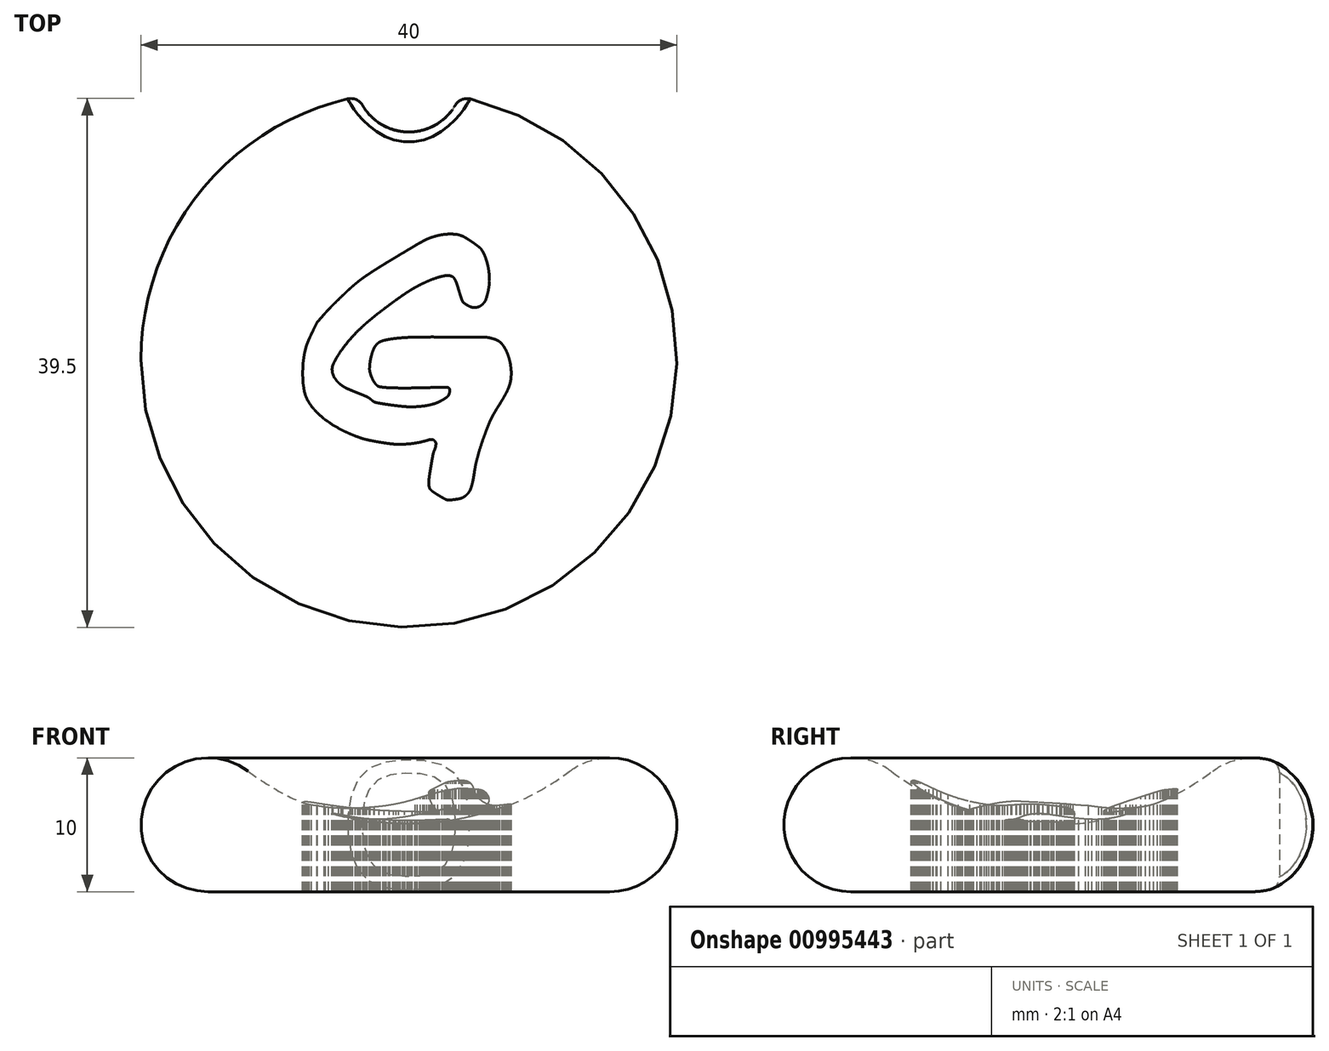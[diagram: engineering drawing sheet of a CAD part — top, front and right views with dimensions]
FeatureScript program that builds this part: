
annotation { "Feature Type Name" : "Feature", "Feature Type Description" : "" }
export const myFeature = defineFeature(function(context is Context, id is Id, definition is map)
    precondition{}
    {
        {
            var Q0;
            Q0=qCreatedBy(makeId("Front.planeOp"),FACE);
            var sketch = newSketch(context, id + "F0", { "sketchPlane" : qUnion([Q0])});
            skArc(sketch, "E0", {"start": v(-12, 9) * mm, "mid": v(-19.74, 6.58) * mm, "end": v(-15, 0) * mm});
            skArc(sketch, "E1", {"start": v(-12, 9) * mm, "mid": v(-6.32, 6.03) * mm, "end": v(0, 5) * mm});
            skLineSegment(sketch, "E2", {"start": v(-15, 0) * mm, "end": v(0, 0) * mm});
            skLineSegment(sketch, "E3", {"start": v(0, 0) * mm, "end": v(0, 5) * mm});
            skSolve(sketch);
        }
        {
            var Q0;
            Q0=makeQuery(id+"F0.imprint","IMPRINT",FACE,{"disambiguationData":[TD([[makeQuery(id+"F0.imprint","IMPRINT",EDGE,{"derivedFrom":sQuery(id+"F0.wireOp",EDGE,"E0")}),1.0]])]});
            var Q1;
            Q1=sQuery(id+"F0.wireOp",EDGE,"E3");
            revolve(context, id + "F1", {"surfaceOperationType" : NewSurfaceOperationType.NEW, "entities" : qUnion([Q0]), "axis" : qUnion([Q1]), "revolveType" : RevolveType.FULL});
        }
        {
            var Q0;
            Q0=qCreatedBy(makeId("Top.planeOp"),FACE);
            cPlane(context, id + "F2", {"entities" : qUnion([Q0]), "cplaneType" : CPlaneType.OFFSET, "offset" : 10 * mm, "width" : 150 * mm, "height" : 150 * mm});
        }
        {
            var Q0;
            Q0=qCreatedBy(id+"F2.planeOp",FACE);
            var sketch = newSketch(context, id + "F3", { "sketchPlane" : qUnion([Q0])});
            skLineSegment(sketch, "E4", {"start": v(-4381.95, 0) * mm, "end": v(-4381.95, -4381.95) * mm});
            skLineSegment(sketch, "E5", {"start": v(-4381.95, -4381.95) * mm, "end": v(0, -4381.95) * mm});
            skLineSegment(sketch, "E6", {"start": v(0, -4381.95) * mm, "end": v(4381.95, -4381.95) * mm});
            skLineSegment(sketch, "E7", {"start": v(4381.95, -4381.95) * mm, "end": v(4381.95, 0) * mm});
            skLineSegment(sketch, "E8", {"start": v(4381.95, 0) * mm, "end": v(4381.95, 4381.95) * mm});
            skLineSegment(sketch, "E9", {"start": v(4381.95, 4381.95) * mm, "end": v(0, 4381.95) * mm});
            skLineSegment(sketch, "E10", {"start": v(0, 4381.95) * mm, "end": v(-4381.95, 4381.95) * mm});
            skLineSegment(sketch, "E11", {"start": v(-4381.95, 4381.95) * mm, "end": v(-4381.95, 0) * mm});
            skLineSegment(sketch, "E12", {"start": v(3.49, 9.37) * mm, "end": v(3.47, 9.37) * mm});
            skLineSegment(sketch, "E13", {"start": v(3.47, 9.37) * mm, "end": v(3.43, 9.37) * mm});
            skLineSegment(sketch, "E14", {"start": v(3.43, 9.37) * mm, "end": v(3.34, 9.37) * mm});
            skLineSegment(sketch, "E15", {"start": v(3.34, 9.37) * mm, "end": v(3.23, 9.37) * mm});
            skLineSegment(sketch, "E16", {"start": v(3.23, 9.37) * mm, "end": v(3.14, 9.37) * mm});
            skLineSegment(sketch, "E17", {"start": v(3.14, 9.37) * mm, "end": v(3.12, 9.38) * mm});
            skLineSegment(sketch, "E18", {"start": v(3.12, 9.38) * mm, "end": v(3, 9.38) * mm});
            skLineSegment(sketch, "E19", {"start": v(3, 9.38) * mm, "end": v(2.65, 9.36) * mm});
            skLineSegment(sketch, "E20", {"start": v(2.65, 9.36) * mm, "end": v(2.17, 9.27) * mm});
            skLineSegment(sketch, "E21", {"start": v(2.17, 9.27) * mm, "end": v(1.68, 9.13) * mm});
            skLineSegment(sketch, "E22", {"start": v(1.68, 9.13) * mm, "end": v(1.33, 8.99) * mm});
            skLineSegment(sketch, "E23", {"start": v(1.33, 8.99) * mm, "end": v(1.22, 8.93) * mm});
            skLineSegment(sketch, "E24", {"start": v(1.22, 8.93) * mm, "end": v(1.18, 8.91) * mm});
            skLineSegment(sketch, "E25", {"start": v(1.18, 8.91) * mm, "end": v(1.06, 8.85) * mm});
            skLineSegment(sketch, "E26", {"start": v(1.06, 8.85) * mm, "end": v(0.85, 8.74) * mm});
            skLineSegment(sketch, "E27", {"start": v(0.85, 8.74) * mm, "end": v(0.63, 8.6) * mm});
            skLineSegment(sketch, "E28", {"start": v(0.63, 8.6) * mm, "end": v(0.46, 8.51) * mm});
            skLineSegment(sketch, "E29", {"start": v(0.46, 8.51) * mm, "end": v(0.41, 8.48) * mm});
            skLineSegment(sketch, "E30", {"start": v(0.41, 8.48) * mm, "end": v(0.24, 8.38) * mm});
            skLineSegment(sketch, "E31", {"start": v(0.24, 8.38) * mm, "end": v(-0.26, 8.08) * mm});
            skLineSegment(sketch, "E32", {"start": v(-0.26, 8.08) * mm, "end": v(-0.85, 7.73) * mm});
            skLineSegment(sketch, "E33", {"start": v(-0.85, 7.73) * mm, "end": v(-1.37, 7.41) * mm});
            skLineSegment(sketch, "E34", {"start": v(-1.37, 7.41) * mm, "end": v(-1.83, 7.13) * mm});
            skLineSegment(sketch, "E35", {"start": v(-1.83, 7.13) * mm, "end": v(-2.23, 6.89) * mm});
            skLineSegment(sketch, "E36", {"start": v(-2.23, 6.89) * mm, "end": v(-2.57, 6.67) * mm});
            skLineSegment(sketch, "E37", {"start": v(-2.57, 6.67) * mm, "end": v(-2.88, 6.47) * mm});
            skLineSegment(sketch, "E38", {"start": v(-2.88, 6.47) * mm, "end": v(-3.15, 6.3) * mm});
            skLineSegment(sketch, "E39", {"start": v(-3.15, 6.3) * mm, "end": v(-3.4, 6.12) * mm});
            skLineSegment(sketch, "E40", {"start": v(-3.4, 6.12) * mm, "end": v(-3.6, 5.96) * mm});
            skLineSegment(sketch, "E41", {"start": v(-3.6, 5.96) * mm, "end": v(-3.8, 5.8) * mm});
            skLineSegment(sketch, "E42", {"start": v(-3.8, 5.8) * mm, "end": v(-4, 5.65) * mm});
            skLineSegment(sketch, "E43", {"start": v(-4, 5.65) * mm, "end": v(-4.19, 5.49) * mm});
            skLineSegment(sketch, "E44", {"start": v(-4.19, 5.49) * mm, "end": v(-4.38, 5.32) * mm});
            skLineSegment(sketch, "E45", {"start": v(-4.38, 5.32) * mm, "end": v(-4.59, 5.13) * mm});
            skLineSegment(sketch, "E46", {"start": v(-4.59, 5.13) * mm, "end": v(-4.75, 4.97) * mm});
            skLineSegment(sketch, "E47", {"start": v(-4.75, 4.97) * mm, "end": v(-4.8, 4.92) * mm});
            skLineSegment(sketch, "E48", {"start": v(-4.8, 4.92) * mm, "end": v(-4.92, 4.82) * mm});
            skLineSegment(sketch, "E49", {"start": v(-4.92, 4.82) * mm, "end": v(-5.25, 4.5) * mm});
            skLineSegment(sketch, "E50", {"start": v(-5.25, 4.5) * mm, "end": v(-5.65, 4.1) * mm});
            skLineSegment(sketch, "E51", {"start": v(-5.65, 4.1) * mm, "end": v(-6, 3.73) * mm});
            skLineSegment(sketch, "E52", {"start": v(-6, 3.73) * mm, "end": v(-6.23, 3.48) * mm});
            skLineSegment(sketch, "E53", {"start": v(-6.23, 3.48) * mm, "end": v(-6.3, 3.4) * mm});
            skLineSegment(sketch, "E54", {"start": v(-6.3, 3.4) * mm, "end": v(-6.87, 2.75) * mm});
            skLineSegment(sketch, "E55", {"start": v(-6.87, 2.75) * mm, "end": v(-7.17, 2.13) * mm});
            skLineSegment(sketch, "E56", {"start": v(-7.17, 2.13) * mm, "end": v(-7.2, 2.06) * mm});
            skLineSegment(sketch, "E57", {"start": v(-7.2, 2.06) * mm, "end": v(-7.3, 1.84) * mm});
            skLineSegment(sketch, "E58", {"start": v(-7.3, 1.84) * mm, "end": v(-7.42, 1.6) * mm});
            skLineSegment(sketch, "E59", {"start": v(-7.42, 1.6) * mm, "end": v(-7.5, 1.4) * mm});
            skLineSegment(sketch, "E60", {"start": v(-7.5, 1.4) * mm, "end": v(-7.57, 1.23) * mm});
            skLineSegment(sketch, "E61", {"start": v(-7.57, 1.23) * mm, "end": v(-7.63, 1.07) * mm});
            skLineSegment(sketch, "E62", {"start": v(-7.63, 1.07) * mm, "end": v(-7.68, 0.92) * mm});
            skLineSegment(sketch, "E63", {"start": v(-7.68, 0.92) * mm, "end": v(-7.72, 0.75) * mm});
            skLineSegment(sketch, "E64", {"start": v(-7.72, 0.75) * mm, "end": v(-7.76, 0.6) * mm});
            skLineSegment(sketch, "E65", {"start": v(-7.76, 0.6) * mm, "end": v(-7.77, 0.56) * mm});
            skLineSegment(sketch, "E66", {"start": v(-7.77, 0.56) * mm, "end": v(-7.81, 0.37) * mm});
            skLineSegment(sketch, "E67", {"start": v(-7.81, 0.37) * mm, "end": v(-7.9, -0.22) * mm});
            skLineSegment(sketch, "E68", {"start": v(-7.9, -0.22) * mm, "end": v(-7.93, -1.05) * mm});
            skLineSegment(sketch, "E69", {"start": v(-7.93, -1.05) * mm, "end": v(-7.89, -1.84) * mm});
            skLineSegment(sketch, "E70", {"start": v(-7.89, -1.84) * mm, "end": v(-7.8, -2.37) * mm});
            skLineSegment(sketch, "E71", {"start": v(-7.8, -2.37) * mm, "end": v(-7.76, -2.54) * mm});
            skLineSegment(sketch, "E72", {"start": v(-7.76, -2.54) * mm, "end": v(-7.72, -2.67) * mm});
            skLineSegment(sketch, "E73", {"start": v(-7.72, -2.67) * mm, "end": v(-7.57, -3.03) * mm});
            skLineSegment(sketch, "E74", {"start": v(-7.57, -3.03) * mm, "end": v(-7.26, -3.51) * mm});
            skLineSegment(sketch, "E75", {"start": v(-7.26, -3.51) * mm, "end": v(-6.84, -3.98) * mm});
            skLineSegment(sketch, "E76", {"start": v(-6.84, -3.98) * mm, "end": v(-6.33, -4.43) * mm});
            skLineSegment(sketch, "E77", {"start": v(-6.33, -4.43) * mm, "end": v(-5.73, -4.85) * mm});
            skLineSegment(sketch, "E78", {"start": v(-5.73, -4.85) * mm, "end": v(-5.05, -5.24) * mm});
            skLineSegment(sketch, "E79", {"start": v(-5.05, -5.24) * mm, "end": v(-4.3, -5.6) * mm});
            skLineSegment(sketch, "E80", {"start": v(-4.3, -5.6) * mm, "end": v(-3.7, -5.82) * mm});
            skLineSegment(sketch, "E81", {"start": v(-3.7, -5.82) * mm, "end": v(-3.49, -5.9) * mm});
            skLineSegment(sketch, "E82", {"start": v(-3.49, -5.9) * mm, "end": v(-3.43, -5.91) * mm});
            skLineSegment(sketch, "E83", {"start": v(-3.43, -5.91) * mm, "end": v(-3.26, -5.96) * mm});
            skLineSegment(sketch, "E84", {"start": v(-3.26, -5.96) * mm, "end": v(-2.95, -6.03) * mm});
            skLineSegment(sketch, "E85", {"start": v(-2.95, -6.03) * mm, "end": v(-2.6, -6.1) * mm});
            skLineSegment(sketch, "E86", {"start": v(-2.6, -6.1) * mm, "end": v(-2.22, -6.16) * mm});
            skLineSegment(sketch, "E87", {"start": v(-2.22, -6.16) * mm, "end": v(-1.83, -6.23) * mm});
            skLineSegment(sketch, "E88", {"start": v(-1.83, -6.23) * mm, "end": v(-1.47, -6.28) * mm});
            skLineSegment(sketch, "E89", {"start": v(-1.47, -6.28) * mm, "end": v(-1.15, -6.31) * mm});
            skLineSegment(sketch, "E90", {"start": v(-1.15, -6.31) * mm, "end": v(-0.97, -6.33) * mm});
            skLineSegment(sketch, "E91", {"start": v(-0.97, -6.33) * mm, "end": v(-0.9, -6.33) * mm});
            skLineSegment(sketch, "E92", {"start": v(-0.9, -6.33) * mm, "end": v(-0.76, -6.33) * mm});
            skLineSegment(sketch, "E93", {"start": v(-0.76, -6.33) * mm, "end": v(-0.31, -6.32) * mm});
            skLineSegment(sketch, "E94", {"start": v(-0.31, -6.32) * mm, "end": v(0.25, -6.28) * mm});
            skLineSegment(sketch, "E95", {"start": v(0.25, -6.28) * mm, "end": v(0.78, -6.19) * mm});
            skLineSegment(sketch, "E96", {"start": v(0.78, -6.19) * mm, "end": v(1.19, -6.09) * mm});
            skLineSegment(sketch, "E97", {"start": v(1.19, -6.09) * mm, "end": v(1.32, -6.05) * mm});
            skLineSegment(sketch, "E98", {"start": v(1.32, -6.05) * mm, "end": v(1.37, -6.04) * mm});
            skLineSegment(sketch, "E99", {"start": v(1.37, -6.04) * mm, "end": v(1.5, -6) * mm});
            skLineSegment(sketch, "E100", {"start": v(1.5, -6) * mm, "end": v(1.63, -5.97) * mm});
            skLineSegment(sketch, "E101", {"start": v(1.63, -5.97) * mm, "end": v(1.73, -5.97) * mm});
            skLineSegment(sketch, "E102", {"start": v(1.73, -5.97) * mm, "end": v(1.78, -5.98) * mm});
            skLineSegment(sketch, "E103", {"start": v(1.78, -5.98) * mm, "end": v(1.8, -5.99) * mm});
            skLineSegment(sketch, "E104", {"start": v(1.8, -5.99) * mm, "end": v(1.84, -6) * mm});
            skLineSegment(sketch, "E105", {"start": v(1.84, -6) * mm, "end": v(1.95, -6.09) * mm});
            skLineSegment(sketch, "E106", {"start": v(1.95, -6.09) * mm, "end": v(2.02, -6.25) * mm});
            skLineSegment(sketch, "E107", {"start": v(2.02, -6.25) * mm, "end": v(2.01, -6.47) * mm});
            skLineSegment(sketch, "E108", {"start": v(2.01, -6.47) * mm, "end": v(1.95, -6.66) * mm});
            skLineSegment(sketch, "E109", {"start": v(1.95, -6.66) * mm, "end": v(1.92, -6.72) * mm});
            skLineSegment(sketch, "E110", {"start": v(1.92, -6.72) * mm, "end": v(1.92, -6.74) * mm});
            skLineSegment(sketch, "E111", {"start": v(1.92, -6.74) * mm, "end": v(1.9, -6.8) * mm});
            skLineSegment(sketch, "E112", {"start": v(1.9, -6.8) * mm, "end": v(1.86, -6.87) * mm});
            skLineSegment(sketch, "E113", {"start": v(1.86, -6.87) * mm, "end": v(1.83, -6.97) * mm});
            skLineSegment(sketch, "E114", {"start": v(1.83, -6.97) * mm, "end": v(1.8, -7.09) * mm});
            skLineSegment(sketch, "E115", {"start": v(1.8, -7.09) * mm, "end": v(1.78, -7.24) * mm});
            skLineSegment(sketch, "E116", {"start": v(1.78, -7.24) * mm, "end": v(1.74, -7.43) * mm});
            skLineSegment(sketch, "E117", {"start": v(1.74, -7.43) * mm, "end": v(1.7, -7.67) * mm});
            skLineSegment(sketch, "E118", {"start": v(1.7, -7.67) * mm, "end": v(1.66, -7.9) * mm});
            skLineSegment(sketch, "E119", {"start": v(1.66, -7.9) * mm, "end": v(1.65, -7.98) * mm});
            skLineSegment(sketch, "E120", {"start": v(1.65, -7.98) * mm, "end": v(1.63, -8.07) * mm});
            skLineSegment(sketch, "E121", {"start": v(1.63, -8.07) * mm, "end": v(1.59, -8.34) * mm});
            skLineSegment(sketch, "E122", {"start": v(1.59, -8.34) * mm, "end": v(1.54, -8.64) * mm});
            skLineSegment(sketch, "E123", {"start": v(1.54, -8.64) * mm, "end": v(1.5, -8.88) * mm});
            skLineSegment(sketch, "E124", {"start": v(1.5, -8.88) * mm, "end": v(1.5, -9.06) * mm});
            skLineSegment(sketch, "E125", {"start": v(1.5, -9.06) * mm, "end": v(1.48, -9.21) * mm});
            skLineSegment(sketch, "E126", {"start": v(1.48, -9.21) * mm, "end": v(1.49, -9.34) * mm});
            skLineSegment(sketch, "E127", {"start": v(1.49, -9.34) * mm, "end": v(1.5, -9.44) * mm});
            skLineSegment(sketch, "E128", {"start": v(1.5, -9.44) * mm, "end": v(1.52, -9.52) * mm});
            skLineSegment(sketch, "E129", {"start": v(1.52, -9.52) * mm, "end": v(1.53, -9.55) * mm});
            skLineSegment(sketch, "E130", {"start": v(1.53, -9.55) * mm, "end": v(1.54, -9.57) * mm});
            skLineSegment(sketch, "E131", {"start": v(1.54, -9.57) * mm, "end": v(1.56, -9.64) * mm});
            skLineSegment(sketch, "E132", {"start": v(1.56, -9.64) * mm, "end": v(1.61, -9.72) * mm});
            skLineSegment(sketch, "E133", {"start": v(1.61, -9.72) * mm, "end": v(1.7, -9.8) * mm});
            skLineSegment(sketch, "E134", {"start": v(1.7, -9.8) * mm, "end": v(1.8, -9.88) * mm});
            skLineSegment(sketch, "E135", {"start": v(1.8, -9.88) * mm, "end": v(1.85, -9.9) * mm});
            skLineSegment(sketch, "E136", {"start": v(1.85, -9.9) * mm, "end": v(1.92, -9.96) * mm});
            skLineSegment(sketch, "E137", {"start": v(1.92, -9.96) * mm, "end": v(2.16, -10.11) * mm});
            skLineSegment(sketch, "E138", {"start": v(2.16, -10.11) * mm, "end": v(2.47, -10.3) * mm});
            skLineSegment(sketch, "E139", {"start": v(2.47, -10.3) * mm, "end": v(2.72, -10.43) * mm});
            skLineSegment(sketch, "E140", {"start": v(2.72, -10.43) * mm, "end": v(2.84, -10.49) * mm});
            skLineSegment(sketch, "E141", {"start": v(2.84, -10.49) * mm, "end": v(2.88, -10.5) * mm});
            skLineSegment(sketch, "E142", {"start": v(2.88, -10.5) * mm, "end": v(2.9, -10.5) * mm});
            skLineSegment(sketch, "E143", {"start": v(2.9, -10.5) * mm, "end": v(2.97, -10.5) * mm});
            skLineSegment(sketch, "E144", {"start": v(2.97, -10.5) * mm, "end": v(3.1, -10.49) * mm});
            skLineSegment(sketch, "E145", {"start": v(3.1, -10.49) * mm, "end": v(3.28, -10.47) * mm});
            skLineSegment(sketch, "E146", {"start": v(3.28, -10.47) * mm, "end": v(3.43, -10.45) * mm});
            skLineSegment(sketch, "E147", {"start": v(3.43, -10.45) * mm, "end": v(3.47, -10.45) * mm});
            skLineSegment(sketch, "E148", {"start": v(3.47, -10.45) * mm, "end": v(3.54, -10.44) * mm});
            skLineSegment(sketch, "E149", {"start": v(3.54, -10.44) * mm, "end": v(3.74, -10.4) * mm});
            skLineSegment(sketch, "E150", {"start": v(3.74, -10.4) * mm, "end": v(3.9, -10.36) * mm});
            skLineSegment(sketch, "E151", {"start": v(3.9, -10.36) * mm, "end": v(4.03, -10.3) * mm});
            skLineSegment(sketch, "E152", {"start": v(4.03, -10.3) * mm, "end": v(4.13, -10.24) * mm});
            skLineSegment(sketch, "E153", {"start": v(4.13, -10.24) * mm, "end": v(4.17, -10.22) * mm});
            skLineSegment(sketch, "E154", {"start": v(4.17, -10.22) * mm, "end": v(4.2, -10.2) * mm});
            skLineSegment(sketch, "E155", {"start": v(4.2, -10.2) * mm, "end": v(4.3, -10.11) * mm});
            skLineSegment(sketch, "E156", {"start": v(4.3, -10.11) * mm, "end": v(4.43, -9.99) * mm});
            skLineSegment(sketch, "E157", {"start": v(4.43, -9.99) * mm, "end": v(4.53, -9.84) * mm});
            skLineSegment(sketch, "E158", {"start": v(4.53, -9.84) * mm, "end": v(4.62, -9.66) * mm});
            skLineSegment(sketch, "E159", {"start": v(4.62, -9.66) * mm, "end": v(4.7, -9.43) * mm});
            skLineSegment(sketch, "E160", {"start": v(4.7, -9.43) * mm, "end": v(4.76, -9.16) * mm});
            skLineSegment(sketch, "E161", {"start": v(4.76, -9.16) * mm, "end": v(4.82, -8.84) * mm});
            skLineSegment(sketch, "E162", {"start": v(4.82, -8.84) * mm, "end": v(4.87, -8.55) * mm});
            skLineSegment(sketch, "E163", {"start": v(4.87, -8.55) * mm, "end": v(4.88, -8.46) * mm});
            skLineSegment(sketch, "E164", {"start": v(4.88, -8.46) * mm, "end": v(4.9, -8.28) * mm});
            skLineSegment(sketch, "E165", {"start": v(4.9, -8.28) * mm, "end": v(5, -7.74) * mm});
            skLineSegment(sketch, "E166", {"start": v(5, -7.74) * mm, "end": v(5.2, -6.98) * mm});
            skLineSegment(sketch, "E167", {"start": v(5.2, -6.98) * mm, "end": v(5.48, -6.12) * mm});
            skLineSegment(sketch, "E168", {"start": v(5.48, -6.12) * mm, "end": v(5.75, -5.36) * mm});
            skLineSegment(sketch, "E169", {"start": v(5.75, -5.36) * mm, "end": v(5.85, -5.1) * mm});
            skLineSegment(sketch, "E170", {"start": v(5.85, -5.1) * mm, "end": v(5.87, -5.05) * mm});
            skLineSegment(sketch, "E171", {"start": v(5.87, -5.05) * mm, "end": v(5.94, -4.88) * mm});
            skLineSegment(sketch, "E172", {"start": v(5.94, -4.88) * mm, "end": v(6.02, -4.68) * mm});
            skLineSegment(sketch, "E173", {"start": v(6.02, -4.68) * mm, "end": v(6.1, -4.5) * mm});
            skLineSegment(sketch, "E174", {"start": v(6.1, -4.5) * mm, "end": v(6.2, -4.3) * mm});
            skLineSegment(sketch, "E175", {"start": v(6.2, -4.3) * mm, "end": v(6.3, -4.12) * mm});
            skLineSegment(sketch, "E176", {"start": v(6.3, -4.12) * mm, "end": v(6.42, -3.9) * mm});
            skLineSegment(sketch, "E177", {"start": v(6.42, -3.9) * mm, "end": v(6.57, -3.67) * mm});
            skLineSegment(sketch, "E178", {"start": v(6.57, -3.67) * mm, "end": v(6.7, -3.46) * mm});
            skLineSegment(sketch, "E179", {"start": v(6.7, -3.46) * mm, "end": v(6.74, -3.39) * mm});
            skLineSegment(sketch, "E180", {"start": v(6.74, -3.39) * mm, "end": v(6.8, -3.29) * mm});
            skLineSegment(sketch, "E181", {"start": v(6.8, -3.29) * mm, "end": v(7, -2.98) * mm});
            skLineSegment(sketch, "E182", {"start": v(7, -2.98) * mm, "end": v(7.2, -2.63) * mm});
            skLineSegment(sketch, "E183", {"start": v(7.2, -2.63) * mm, "end": v(7.35, -2.32) * mm});
            skLineSegment(sketch, "E184", {"start": v(7.35, -2.32) * mm, "end": v(7.47, -2.05) * mm});
            skLineSegment(sketch, "E185", {"start": v(7.47, -2.05) * mm, "end": v(7.55, -1.8) * mm});
            skLineSegment(sketch, "E186", {"start": v(7.55, -1.8) * mm, "end": v(7.6, -1.54) * mm});
            skLineSegment(sketch, "E187", {"start": v(7.6, -1.54) * mm, "end": v(7.63, -1.29) * mm});
            skLineSegment(sketch, "E188", {"start": v(7.63, -1.29) * mm, "end": v(7.64, -1.09) * mm});
            skLineSegment(sketch, "E189", {"start": v(7.64, -1.09) * mm, "end": v(7.64, -1.02) * mm});
            skLineSegment(sketch, "E190", {"start": v(7.64, -1.02) * mm, "end": v(7.64, -0.93) * mm});
            skLineSegment(sketch, "E191", {"start": v(7.64, -0.93) * mm, "end": v(7.63, -0.66) * mm});
            skLineSegment(sketch, "E192", {"start": v(7.63, -0.66) * mm, "end": v(7.58, -0.3) * mm});
            skLineSegment(sketch, "E193", {"start": v(7.58, -0.3) * mm, "end": v(7.5, 0.05) * mm});
            skLineSegment(sketch, "E194", {"start": v(7.5, 0.05) * mm, "end": v(7.39, 0.38) * mm});
            skLineSegment(sketch, "E195", {"start": v(7.39, 0.38) * mm, "end": v(7.26, 0.69) * mm});
            skLineSegment(sketch, "E196", {"start": v(7.26, 0.69) * mm, "end": v(7.1, 0.95) * mm});
            skLineSegment(sketch, "E197", {"start": v(7.1, 0.95) * mm, "end": v(6.94, 1.18) * mm});
            skLineSegment(sketch, "E198", {"start": v(6.94, 1.18) * mm, "end": v(6.81, 1.3) * mm});
            skLineSegment(sketch, "E199", {"start": v(6.81, 1.3) * mm, "end": v(6.76, 1.35) * mm});
            skLineSegment(sketch, "E200", {"start": v(6.76, 1.35) * mm, "end": v(6.74, 1.36) * mm});
            skLineSegment(sketch, "E201", {"start": v(6.74, 1.36) * mm, "end": v(6.67, 1.4) * mm});
            skLineSegment(sketch, "E202", {"start": v(6.67, 1.4) * mm, "end": v(6.55, 1.46) * mm});
            skLineSegment(sketch, "E203", {"start": v(6.55, 1.46) * mm, "end": v(6.41, 1.52) * mm});
            skLineSegment(sketch, "E204", {"start": v(6.41, 1.52) * mm, "end": v(6.27, 1.56) * mm});
            skLineSegment(sketch, "E205", {"start": v(6.27, 1.56) * mm, "end": v(6.23, 1.57) * mm});
            skLineSegment(sketch, "E206", {"start": v(6.23, 1.57) * mm, "end": v(6.2, 1.58) * mm});
            skLineSegment(sketch, "E207", {"start": v(6.2, 1.58) * mm, "end": v(6.1, 1.6) * mm});
            skLineSegment(sketch, "E208", {"start": v(6.1, 1.6) * mm, "end": v(6, 1.63) * mm});
            skLineSegment(sketch, "E209", {"start": v(6, 1.63) * mm, "end": v(5.9, 1.65) * mm});
            skLineSegment(sketch, "E210", {"start": v(5.9, 1.65) * mm, "end": v(5.8, 1.66) * mm});
            skLineSegment(sketch, "E211", {"start": v(5.8, 1.66) * mm, "end": v(5.69, 1.67) * mm});
            skLineSegment(sketch, "E212", {"start": v(5.69, 1.67) * mm, "end": v(5.54, 1.67) * mm});
            skLineSegment(sketch, "E213", {"start": v(5.54, 1.67) * mm, "end": v(5.35, 1.67) * mm});
            skLineSegment(sketch, "E214", {"start": v(5.35, 1.67) * mm, "end": v(5.17, 1.67) * mm});
            skLineSegment(sketch, "E215", {"start": v(5.17, 1.67) * mm, "end": v(5.11, 1.67) * mm});
            skLineSegment(sketch, "E216", {"start": v(5.11, 1.67) * mm, "end": v(5.07, 1.67) * mm});
            skLineSegment(sketch, "E217", {"start": v(5.07, 1.67) * mm, "end": v(4.93, 1.67) * mm});
            skLineSegment(sketch, "E218", {"start": v(4.93, 1.67) * mm, "end": v(4.69, 1.67) * mm});
            skLineSegment(sketch, "E219", {"start": v(4.69, 1.67) * mm, "end": v(4.4, 1.67) * mm});
            skLineSegment(sketch, "E220", {"start": v(4.4, 1.67) * mm, "end": v(4.07, 1.67) * mm});
            skLineSegment(sketch, "E221", {"start": v(4.07, 1.67) * mm, "end": v(3.72, 1.67) * mm});
            skLineSegment(sketch, "E222", {"start": v(3.72, 1.67) * mm, "end": v(3.35, 1.68) * mm});
            skLineSegment(sketch, "E223", {"start": v(3.35, 1.68) * mm, "end": v(2.97, 1.68) * mm});
            skLineSegment(sketch, "E224", {"start": v(2.97, 1.68) * mm, "end": v(2.7, 1.68) * mm});
            skLineSegment(sketch, "E225", {"start": v(2.7, 1.68) * mm, "end": v(2.6, 1.68) * mm});
            skLineSegment(sketch, "E226", {"start": v(2.6, 1.68) * mm, "end": v(2.4, 1.68) * mm});
            skLineSegment(sketch, "E227", {"start": v(2.4, 1.68) * mm, "end": v(1.8, 1.69) * mm});
            skLineSegment(sketch, "E228", {"start": v(1.8, 1.69) * mm, "end": v(1.12, 1.69) * mm});
            skLineSegment(sketch, "E229", {"start": v(1.12, 1.69) * mm, "end": v(0.53, 1.68) * mm});
            skLineSegment(sketch, "E230", {"start": v(0.53, 1.68) * mm, "end": v(0.01, 1.66) * mm});
            skLineSegment(sketch, "E231", {"start": v(0.01, 1.66) * mm, "end": v(-0.44, 1.63) * mm});
            skLineSegment(sketch, "E232", {"start": v(-0.44, 1.63) * mm, "end": v(-0.84, 1.6) * mm});
            skLineSegment(sketch, "E233", {"start": v(-0.84, 1.6) * mm, "end": v(-1.22, 1.55) * mm});
            skLineSegment(sketch, "E234", {"start": v(-1.22, 1.55) * mm, "end": v(-1.48, 1.51) * mm});
            skLineSegment(sketch, "E235", {"start": v(-1.48, 1.51) * mm, "end": v(-1.57, 1.5) * mm});
            skLineSegment(sketch, "E236", {"start": v(-1.57, 1.5) * mm, "end": v(-1.67, 1.48) * mm});
            skLineSegment(sketch, "E237", {"start": v(-1.67, 1.48) * mm, "end": v(-1.95, 1.4) * mm});
            skLineSegment(sketch, "E238", {"start": v(-1.95, 1.4) * mm, "end": v(-2.22, 1.3) * mm});
            skLineSegment(sketch, "E239", {"start": v(-2.22, 1.3) * mm, "end": v(-2.4, 1.14) * mm});
            skLineSegment(sketch, "E240", {"start": v(-2.4, 1.14) * mm, "end": v(-2.53, 0.98) * mm});
            skLineSegment(sketch, "E241", {"start": v(-2.53, 0.98) * mm, "end": v(-2.56, 0.92) * mm});
            skLineSegment(sketch, "E242", {"start": v(-2.56, 0.92) * mm, "end": v(-2.61, 0.83) * mm});
            skLineSegment(sketch, "E243", {"start": v(-2.61, 0.83) * mm, "end": v(-2.73, 0.52) * mm});
            skLineSegment(sketch, "E244", {"start": v(-2.73, 0.52) * mm, "end": v(-2.86, 0.04) * mm});
            skLineSegment(sketch, "E245", {"start": v(-2.86, 0.04) * mm, "end": v(-2.93, -0.44) * mm});
            skLineSegment(sketch, "E246", {"start": v(-2.93, -0.44) * mm, "end": v(-2.94, -0.74) * mm});
            skLineSegment(sketch, "E247", {"start": v(-2.94, -0.74) * mm, "end": v(-2.92, -0.83) * mm});
            skLineSegment(sketch, "E248", {"start": v(-2.92, -0.83) * mm, "end": v(-2.9, -0.93) * mm});
            skLineSegment(sketch, "E249", {"start": v(-2.9, -0.93) * mm, "end": v(-2.82, -1.21) * mm});
            skLineSegment(sketch, "E250", {"start": v(-2.82, -1.21) * mm, "end": v(-2.66, -1.57) * mm});
            skLineSegment(sketch, "E251", {"start": v(-2.66, -1.57) * mm, "end": v(-2.47, -1.85) * mm});
            skLineSegment(sketch, "E252", {"start": v(-2.47, -1.85) * mm, "end": v(-2.33, -1.98) * mm});
            skLineSegment(sketch, "E253", {"start": v(-2.33, -1.98) * mm, "end": v(-2.28, -2) * mm});
            skLineSegment(sketch, "E254", {"start": v(-2.28, -2) * mm, "end": v(-2.24, -2.02) * mm});
            skLineSegment(sketch, "E255", {"start": v(-2.24, -2.02) * mm, "end": v(-2.11, -2.04) * mm});
            skLineSegment(sketch, "E256", {"start": v(-2.11, -2.04) * mm, "end": v(-1.86, -2.08) * mm});
            skLineSegment(sketch, "E257", {"start": v(-1.86, -2.08) * mm, "end": v(-1.53, -2.1) * mm});
            skLineSegment(sketch, "E258", {"start": v(-1.53, -2.1) * mm, "end": v(-1.11, -2.12) * mm});
            skLineSegment(sketch, "E259", {"start": v(-1.11, -2.12) * mm, "end": v(-0.62, -2.13) * mm});
            skLineSegment(sketch, "E260", {"start": v(-0.62, -2.13) * mm, "end": v(-0.05, -2.13) * mm});
            skLineSegment(sketch, "E261", {"start": v(-0.05, -2.13) * mm, "end": v(0.6, -2.12) * mm});
            skLineSegment(sketch, "E262", {"start": v(0.6, -2.12) * mm, "end": v(1.14, -2.1) * mm});
            skLineSegment(sketch, "E263", {"start": v(1.14, -2.1) * mm, "end": v(1.32, -2.1) * mm});
            skLineSegment(sketch, "E264", {"start": v(1.32, -2.1) * mm, "end": v(1.44, -2.1) * mm});
            skLineSegment(sketch, "E265", {"start": v(1.44, -2.1) * mm, "end": v(1.82, -2.08) * mm});
            skLineSegment(sketch, "E266", {"start": v(1.82, -2.08) * mm, "end": v(2.27, -2.07) * mm});
            skLineSegment(sketch, "E267", {"start": v(2.27, -2.07) * mm, "end": v(2.6, -2.07) * mm});
            skLineSegment(sketch, "E268", {"start": v(2.6, -2.07) * mm, "end": v(2.75, -2.07) * mm});
            skLineSegment(sketch, "E269", {"start": v(2.75, -2.07) * mm, "end": v(2.78, -2.07) * mm});
            skLineSegment(sketch, "E270", {"start": v(2.78, -2.07) * mm, "end": v(2.8, -2.07) * mm});
            skLineSegment(sketch, "E271", {"start": v(2.8, -2.07) * mm, "end": v(2.9, -2.08) * mm});
            skLineSegment(sketch, "E272", {"start": v(2.9, -2.08) * mm, "end": v(2.96, -2.1) * mm});
            skLineSegment(sketch, "E273", {"start": v(2.96, -2.1) * mm, "end": v(3, -2.13) * mm});
            skLineSegment(sketch, "E274", {"start": v(3, -2.13) * mm, "end": v(3.02, -2.17) * mm});
            skLineSegment(sketch, "E275", {"start": v(3.02, -2.17) * mm, "end": v(3.02, -2.19) * mm});
            skLineSegment(sketch, "E276", {"start": v(3.02, -2.19) * mm, "end": v(3.04, -2.22) * mm});
            skLineSegment(sketch, "E277", {"start": v(3.04, -2.22) * mm, "end": v(3.05, -2.3) * mm});
            skLineSegment(sketch, "E278", {"start": v(3.05, -2.3) * mm, "end": v(3.04, -2.45) * mm});
            skLineSegment(sketch, "E279", {"start": v(3.04, -2.45) * mm, "end": v(3, -2.59) * mm});
            skLineSegment(sketch, "E280", {"start": v(3, -2.59) * mm, "end": v(2.96, -2.68) * mm});
            skLineSegment(sketch, "E281", {"start": v(2.96, -2.68) * mm, "end": v(2.94, -2.7) * mm});
            skLineSegment(sketch, "E282", {"start": v(2.94, -2.7) * mm, "end": v(2.9, -2.74) * mm});
            skLineSegment(sketch, "E283", {"start": v(2.9, -2.74) * mm, "end": v(2.8, -2.84) * mm});
            skLineSegment(sketch, "E284", {"start": v(2.8, -2.84) * mm, "end": v(2.58, -2.99) * mm});
            skLineSegment(sketch, "E285", {"start": v(2.58, -2.99) * mm, "end": v(2.31, -3.13) * mm});
            skLineSegment(sketch, "E286", {"start": v(2.31, -3.13) * mm, "end": v(2.12, -3.22) * mm});
            skLineSegment(sketch, "E287", {"start": v(2.12, -3.22) * mm, "end": v(2.05, -3.24) * mm});
            skLineSegment(sketch, "E288", {"start": v(2.05, -3.24) * mm, "end": v(1.94, -3.29) * mm});
            skLineSegment(sketch, "E289", {"start": v(1.94, -3.29) * mm, "end": v(1.6, -3.38) * mm});
            skLineSegment(sketch, "E290", {"start": v(1.6, -3.38) * mm, "end": v(1.1, -3.47) * mm});
            skLineSegment(sketch, "E291", {"start": v(1.1, -3.47) * mm, "end": v(0.56, -3.52) * mm});
            skLineSegment(sketch, "E292", {"start": v(0.56, -3.52) * mm, "end": v(0.1, -3.53) * mm});
            skLineSegment(sketch, "E293", {"start": v(0.1, -3.53) * mm, "end": v(-0.06, -3.53) * mm});
            skLineSegment(sketch, "E294", {"start": v(-0.06, -3.53) * mm, "end": v(-0.12, -3.53) * mm});
            skLineSegment(sketch, "E295", {"start": v(-0.12, -3.53) * mm, "end": v(-0.3, -3.51) * mm});
            skLineSegment(sketch, "E296", {"start": v(-0.3, -3.51) * mm, "end": v(-0.63, -3.48) * mm});
            skLineSegment(sketch, "E297", {"start": v(-0.63, -3.48) * mm, "end": v(-1, -3.44) * mm});
            skLineSegment(sketch, "E298", {"start": v(-1, -3.44) * mm, "end": v(-1.4, -3.38) * mm});
            skLineSegment(sketch, "E299", {"start": v(-1.4, -3.38) * mm, "end": v(-1.79, -3.33) * mm});
            skLineSegment(sketch, "E300", {"start": v(-1.79, -3.33) * mm, "end": v(-2.13, -3.27) * mm});
            skLineSegment(sketch, "E301", {"start": v(-2.13, -3.27) * mm, "end": v(-2.4, -3.22) * mm});
            skLineSegment(sketch, "E302", {"start": v(-2.4, -3.22) * mm, "end": v(-2.51, -3.2) * mm});
            skLineSegment(sketch, "E303", {"start": v(-2.51, -3.2) * mm, "end": v(-2.55, -3.18) * mm});
            skLineSegment(sketch, "E304", {"start": v(-2.55, -3.18) * mm, "end": v(-2.57, -3.17) * mm});
            skLineSegment(sketch, "E305", {"start": v(-2.57, -3.17) * mm, "end": v(-2.61, -3.15) * mm});
            skLineSegment(sketch, "E306", {"start": v(-2.61, -3.15) * mm, "end": v(-2.69, -3.1) * mm});
            skLineSegment(sketch, "E307", {"start": v(-2.69, -3.1) * mm, "end": v(-2.77, -3.04) * mm});
            skLineSegment(sketch, "E308", {"start": v(-2.77, -3.04) * mm, "end": v(-2.82, -3) * mm});
            skLineSegment(sketch, "E309", {"start": v(-2.82, -3) * mm, "end": v(-2.84, -2.98) * mm});
            skLineSegment(sketch, "E310", {"start": v(-2.84, -2.98) * mm, "end": v(-2.87, -2.95) * mm});
            skLineSegment(sketch, "E311", {"start": v(-2.87, -2.95) * mm, "end": v(-2.95, -2.88) * mm});
            skLineSegment(sketch, "E312", {"start": v(-2.95, -2.88) * mm, "end": v(-3.1, -2.8) * mm});
            skLineSegment(sketch, "E313", {"start": v(-3.1, -2.8) * mm, "end": v(-3.33, -2.7) * mm});
            skLineSegment(sketch, "E314", {"start": v(-3.33, -2.7) * mm, "end": v(-3.6, -2.58) * mm});
            skLineSegment(sketch, "E315", {"start": v(-3.6, -2.58) * mm, "end": v(-3.7, -2.54) * mm});
            skLineSegment(sketch, "E316", {"start": v(-3.7, -2.54) * mm, "end": v(-3.77, -2.51) * mm});
            skLineSegment(sketch, "E317", {"start": v(-3.77, -2.51) * mm, "end": v(-4, -2.42) * mm});
            skLineSegment(sketch, "E318", {"start": v(-4, -2.42) * mm, "end": v(-4.26, -2.32) * mm});
            skLineSegment(sketch, "E319", {"start": v(-4.26, -2.32) * mm, "end": v(-4.46, -2.23) * mm});
            skLineSegment(sketch, "E320", {"start": v(-4.46, -2.23) * mm, "end": v(-4.61, -2.16) * mm});
            skLineSegment(sketch, "E321", {"start": v(-4.61, -2.16) * mm, "end": v(-4.74, -2.1) * mm});
            skLineSegment(sketch, "E322", {"start": v(-4.74, -2.1) * mm, "end": v(-4.84, -2.04) * mm});
            skLineSegment(sketch, "E323", {"start": v(-4.84, -2.04) * mm, "end": v(-4.95, -1.97) * mm});
            skLineSegment(sketch, "E324", {"start": v(-4.95, -1.97) * mm, "end": v(-5.03, -1.92) * mm});
            skLineSegment(sketch, "E325", {"start": v(-5.03, -1.92) * mm, "end": v(-5.05, -1.9) * mm});
            skLineSegment(sketch, "E326", {"start": v(-5.05, -1.9) * mm, "end": v(-5.14, -1.84) * mm});
            skLineSegment(sketch, "E327", {"start": v(-5.14, -1.84) * mm, "end": v(-5.36, -1.62) * mm});
            skLineSegment(sketch, "E328", {"start": v(-5.36, -1.62) * mm, "end": v(-5.58, -1.32) * mm});
            skLineSegment(sketch, "E329", {"start": v(-5.58, -1.32) * mm, "end": v(-5.7, -0.99) * mm});
            skLineSegment(sketch, "E330", {"start": v(-5.7, -0.99) * mm, "end": v(-5.73, -0.73) * mm});
            skLineSegment(sketch, "E331", {"start": v(-5.73, -0.73) * mm, "end": v(-5.73, -0.65) * mm});
            skLineSegment(sketch, "E332", {"start": v(-5.73, -0.65) * mm, "end": v(-5.72, -0.62) * mm});
            skLineSegment(sketch, "E333", {"start": v(-5.72, -0.62) * mm, "end": v(-5.7, -0.52) * mm});
            skLineSegment(sketch, "E334", {"start": v(-5.7, -0.52) * mm, "end": v(-5.67, -0.4) * mm});
            skLineSegment(sketch, "E335", {"start": v(-5.67, -0.4) * mm, "end": v(-5.6, -0.23) * mm});
            skLineSegment(sketch, "E336", {"start": v(-5.6, -0.23) * mm, "end": v(-5.5, -0.05) * mm});
            skLineSegment(sketch, "E337", {"start": v(-5.5, -0.05) * mm, "end": v(-5.47, 0) * mm});
            skLineSegment(sketch, "E338", {"start": v(-5.47, 0) * mm, "end": v(-5.37, 0.18) * mm});
            skLineSegment(sketch, "E339", {"start": v(-5.37, 0.18) * mm, "end": v(-5.05, 0.67) * mm});
            skLineSegment(sketch, "E340", {"start": v(-5.05, 0.67) * mm, "end": v(-4.54, 1.35) * mm});
            skLineSegment(sketch, "E341", {"start": v(-4.54, 1.35) * mm, "end": v(-3.93, 2.02) * mm});
            skLineSegment(sketch, "E342", {"start": v(-3.93, 2.02) * mm, "end": v(-3.42, 2.51) * mm});
            skLineSegment(sketch, "E343", {"start": v(-3.42, 2.51) * mm, "end": v(-3.25, 2.67) * mm});
            skLineSegment(sketch, "E344", {"start": v(-3.25, 2.67) * mm, "end": v(-3.15, 2.75) * mm});
            skLineSegment(sketch, "E345", {"start": v(-3.15, 2.75) * mm, "end": v(-2.87, 2.98) * mm});
            skLineSegment(sketch, "E346", {"start": v(-2.87, 2.98) * mm, "end": v(-2.43, 3.34) * mm});
            skLineSegment(sketch, "E347", {"start": v(-2.43, 3.34) * mm, "end": v(-1.95, 3.72) * mm});
            skLineSegment(sketch, "E348", {"start": v(-1.95, 3.72) * mm, "end": v(-1.45, 4.1) * mm});
            skLineSegment(sketch, "E349", {"start": v(-1.45, 4.1) * mm, "end": v(-0.95, 4.45) * mm});
            skLineSegment(sketch, "E350", {"start": v(-0.95, 4.45) * mm, "end": v(-0.49, 4.78) * mm});
            skLineSegment(sketch, "E351", {"start": v(-0.49, 4.78) * mm, "end": v(-0.07, 5.06) * mm});
            skLineSegment(sketch, "E352", {"start": v(-0.07, 5.06) * mm, "end": v(0.18, 5.22) * mm});
            skLineSegment(sketch, "E353", {"start": v(0.18, 5.22) * mm, "end": v(0.26, 5.27) * mm});
            skLineSegment(sketch, "E354", {"start": v(0.26, 5.27) * mm, "end": v(0.44, 5.37) * mm});
            skLineSegment(sketch, "E355", {"start": v(0.44, 5.37) * mm, "end": v(0.98, 5.66) * mm});
            skLineSegment(sketch, "E356", {"start": v(0.98, 5.66) * mm, "end": v(1.68, 5.97) * mm});
            skLineSegment(sketch, "E357", {"start": v(1.68, 5.97) * mm, "end": v(2.3, 6.18) * mm});
            skLineSegment(sketch, "E358", {"start": v(2.3, 6.18) * mm, "end": v(2.67, 6.26) * mm});
            skLineSegment(sketch, "E359", {"start": v(2.67, 6.26) * mm, "end": v(2.8, 6.27) * mm});
            skLineSegment(sketch, "E360", {"start": v(2.8, 6.27) * mm, "end": v(2.84, 6.27) * mm});
            skLineSegment(sketch, "E361", {"start": v(2.84, 6.27) * mm, "end": v(2.98, 6.27) * mm});
            skLineSegment(sketch, "E362", {"start": v(2.98, 6.27) * mm, "end": v(3.13, 6.25) * mm});
            skLineSegment(sketch, "E363", {"start": v(3.13, 6.25) * mm, "end": v(3.25, 6.2) * mm});
            skLineSegment(sketch, "E364", {"start": v(3.25, 6.2) * mm, "end": v(3.36, 6.1) * mm});
            skLineSegment(sketch, "E365", {"start": v(3.36, 6.1) * mm, "end": v(3.45, 5.96) * mm});
            skLineSegment(sketch, "E366", {"start": v(3.45, 5.96) * mm, "end": v(3.54, 5.75) * mm});
            skLineSegment(sketch, "E367", {"start": v(3.54, 5.75) * mm, "end": v(3.64, 5.49) * mm});
            skLineSegment(sketch, "E368", {"start": v(3.64, 5.49) * mm, "end": v(3.71, 5.23) * mm});
            skLineSegment(sketch, "E369", {"start": v(3.71, 5.23) * mm, "end": v(3.74, 5.14) * mm});
            skLineSegment(sketch, "E370", {"start": v(3.74, 5.14) * mm, "end": v(3.76, 5.07) * mm});
            skLineSegment(sketch, "E371", {"start": v(3.76, 5.07) * mm, "end": v(3.83, 4.85) * mm});
            skLineSegment(sketch, "E372", {"start": v(3.83, 4.85) * mm, "end": v(3.9, 4.6) * mm});
            skLineSegment(sketch, "E373", {"start": v(3.9, 4.6) * mm, "end": v(3.98, 4.41) * mm});
            skLineSegment(sketch, "E374", {"start": v(3.98, 4.41) * mm, "end": v(4.02, 4.33) * mm});
            skLineSegment(sketch, "E375", {"start": v(4.02, 4.33) * mm, "end": v(4.03, 4.31) * mm});
            skLineSegment(sketch, "E376", {"start": v(4.03, 4.31) * mm, "end": v(4.06, 4.28) * mm});
            skLineSegment(sketch, "E377", {"start": v(4.06, 4.28) * mm, "end": v(4.16, 4.2) * mm});
            skLineSegment(sketch, "E378", {"start": v(4.16, 4.2) * mm, "end": v(4.35, 4.06) * mm});
            skLineSegment(sketch, "E379", {"start": v(4.35, 4.06) * mm, "end": v(4.56, 3.96) * mm});
            skLineSegment(sketch, "E380", {"start": v(4.56, 3.96) * mm, "end": v(4.7, 3.9) * mm});
            skLineSegment(sketch, "E381", {"start": v(4.7, 3.9) * mm, "end": v(4.75, 3.9) * mm});
            skLineSegment(sketch, "E382", {"start": v(4.75, 3.9) * mm, "end": v(4.81, 3.89) * mm});
            skLineSegment(sketch, "E383", {"start": v(4.81, 3.89) * mm, "end": v(5.03, 3.9) * mm});
            skLineSegment(sketch, "E384", {"start": v(5.03, 3.9) * mm, "end": v(5.28, 3.96) * mm});
            skLineSegment(sketch, "E385", {"start": v(5.28, 3.96) * mm, "end": v(5.5, 4.12) * mm});
            skLineSegment(sketch, "E386", {"start": v(5.5, 4.12) * mm, "end": v(5.64, 4.29) * mm});
            skLineSegment(sketch, "E387", {"start": v(5.64, 4.29) * mm, "end": v(5.68, 4.35) * mm});
            skLineSegment(sketch, "E388", {"start": v(5.68, 4.35) * mm, "end": v(5.72, 4.42) * mm});
            skLineSegment(sketch, "E389", {"start": v(5.72, 4.42) * mm, "end": v(5.8, 4.65) * mm});
            skLineSegment(sketch, "E390", {"start": v(5.8, 4.65) * mm, "end": v(5.91, 5.07) * mm});
            skLineSegment(sketch, "E391", {"start": v(5.91, 5.07) * mm, "end": v(6, 5.54) * mm});
            skLineSegment(sketch, "E392", {"start": v(6, 5.54) * mm, "end": v(6.02, 5.85) * mm});
            skLineSegment(sketch, "E393", {"start": v(6.02, 5.85) * mm, "end": v(6.02, 5.96) * mm});
            skLineSegment(sketch, "E394", {"start": v(6.02, 5.96) * mm, "end": v(6.02, 6.04) * mm});
            skLineSegment(sketch, "E395", {"start": v(6.02, 6.04) * mm, "end": v(6, 6.3) * mm});
            skLineSegment(sketch, "E396", {"start": v(6, 6.3) * mm, "end": v(5.96, 6.65) * mm});
            skLineSegment(sketch, "E397", {"start": v(5.96, 6.65) * mm, "end": v(5.9, 6.98) * mm});
            skLineSegment(sketch, "E398", {"start": v(5.9, 6.98) * mm, "end": v(5.82, 7.3) * mm});
            skLineSegment(sketch, "E399", {"start": v(5.82, 7.3) * mm, "end": v(5.73, 7.6) * mm});
            skLineSegment(sketch, "E400", {"start": v(5.73, 7.6) * mm, "end": v(5.61, 7.88) * mm});
            skLineSegment(sketch, "E401", {"start": v(5.61, 7.88) * mm, "end": v(5.5, 8.11) * mm});
            skLineSegment(sketch, "E402", {"start": v(5.5, 8.11) * mm, "end": v(5.4, 8.25) * mm});
            skLineSegment(sketch, "E403", {"start": v(5.4, 8.25) * mm, "end": v(5.36, 8.3) * mm});
            skLineSegment(sketch, "E404", {"start": v(5.36, 8.3) * mm, "end": v(5.34, 8.32) * mm});
            skLineSegment(sketch, "E405", {"start": v(5.34, 8.32) * mm, "end": v(5.27, 8.38) * mm});
            skLineSegment(sketch, "E406", {"start": v(5.27, 8.38) * mm, "end": v(5.14, 8.48) * mm});
            skLineSegment(sketch, "E407", {"start": v(5.14, 8.48) * mm, "end": v(4.97, 8.61) * mm});
            skLineSegment(sketch, "E408", {"start": v(4.97, 8.61) * mm, "end": v(4.78, 8.75) * mm});
            skLineSegment(sketch, "E409", {"start": v(4.78, 8.75) * mm, "end": v(4.58, 8.88) * mm});
            skLineSegment(sketch, "E410", {"start": v(4.58, 8.88) * mm, "end": v(4.38, 9) * mm});
            skLineSegment(sketch, "E411", {"start": v(4.38, 9) * mm, "end": v(4.2, 9.11) * mm});
            skLineSegment(sketch, "E412", {"start": v(4.2, 9.11) * mm, "end": v(4.1, 9.17) * mm});
            skLineSegment(sketch, "E413", {"start": v(4.1, 9.17) * mm, "end": v(4.07, 9.19) * mm});
            skLineSegment(sketch, "E414", {"start": v(4.07, 9.19) * mm, "end": v(4.02, 9.21) * mm});
            skLineSegment(sketch, "E415", {"start": v(4.02, 9.21) * mm, "end": v(3.75, 9.31) * mm});
            skLineSegment(sketch, "E416", {"start": v(3.75, 9.31) * mm, "end": v(3.52, 9.36) * mm});
            skLineSegment(sketch, "E417", {"start": v(3.52, 9.36) * mm, "end": v(3.49, 9.37) * mm});
            skLineSegment(sketch, "E418.0", {"start": v(-7.81, 0.37) * mm, "end": v(7.45, -2.32) * mm, "construction": true});
            skLineSegment(sketch, "E418.1", {"start": v(7.45, -2.32) * mm, "end": v(7.63, -1.29) * mm, "construction": true});
            skSolve(sketch);
        }
        {
            var Q0;
            Q0=makeQuery(id+"F3.imprint","IMPRINT",FACE,{"disambiguationData":[TD([[makeQuery(id+"F3.imprint","IMPRINT",EDGE,{"derivedFrom":sQuery(id+"F3.wireOp",EDGE,"E12")}),1.0]])]});
            extrude(context, id + "F4", {"entities" : qUnion([Q0]), "operationType" : NewBodyOperationType.REMOVE, "oppositeDirection" : true, "depth" : 25 * mm, "offsetDistance" : 25 * mm});
        }
        {
            var Q0;
            Q0=qCreatedBy(makeId("Front.planeOp"),FACE);
            var sketch = newSketch(context, id + "F5", { "sketchPlane" : qUnion([Q0])});
            skCircle(sketch, "E419", {"center": v(-15, 5) * mm, "radius": 4 * mm});
            skSolve(sketch);
        }
        {
            var Q0;
            Q0=sQuery(id+"F5.wireOp",EDGE,"E419");
            var Q1;
            Q1=sQuery(id+"F0.wireOp",EDGE,"E3");
            revolve(context, id + "F6", {"bodyType" : ToolBodyType.SURFACE, "surfaceOperationType" : NewSurfaceOperationType.NEW, "surfaceEntities" : qUnion([Q0]), "axis" : qUnion([Q1]), "revolveType" : RevolveType.FULL});
        }
        {
            var Q0;
            Q0=qCreatedBy(makeId("Top.planeOp"),FACE);
            var sketch = newSketch(context, id + "F7", { "sketchPlane" : qUnion([Q0])});
            skCircle(sketch, "E420", {"center": v(0, 21) * mm, "radius": 4 * mm});
            skSolve(sketch);
        }
        {
            var Q0;
            Q0 = qSketchRegion(id + "F7", true);
            extrude(context, id + "F8", {"entities" : qUnion([Q0]), "operationType" : NewBodyOperationType.REMOVE, "depth" : 25 * mm, "offsetDistance" : 25 * mm});
        }
        {
            var Q0;
            Q0=makeQuery(id+"F8.boolean.opBoolean","INTERSECT",EDGE,{"derivedFrom":[makeQuery(id+"F1.opRevolve","SWEPT_FACE",FACE,{"disambiguationData":[OSD([sQuery(id+"F0.wireOp",EDGE,"E0")])]}),makeQuery(id+"F8.opExtrude","SWEPT_FACE",FACE,{"disambiguationData":[OSD([sQuery(id+"F7.wireOp",EDGE,"E420")])]})]});
            fillet(context, id + "F9", {"entities" : qUnion([Q0]), "radius" : 1 * mm, "tangentPropagation" : true, "allowEdgeOverflow" : false});
        }
    });
